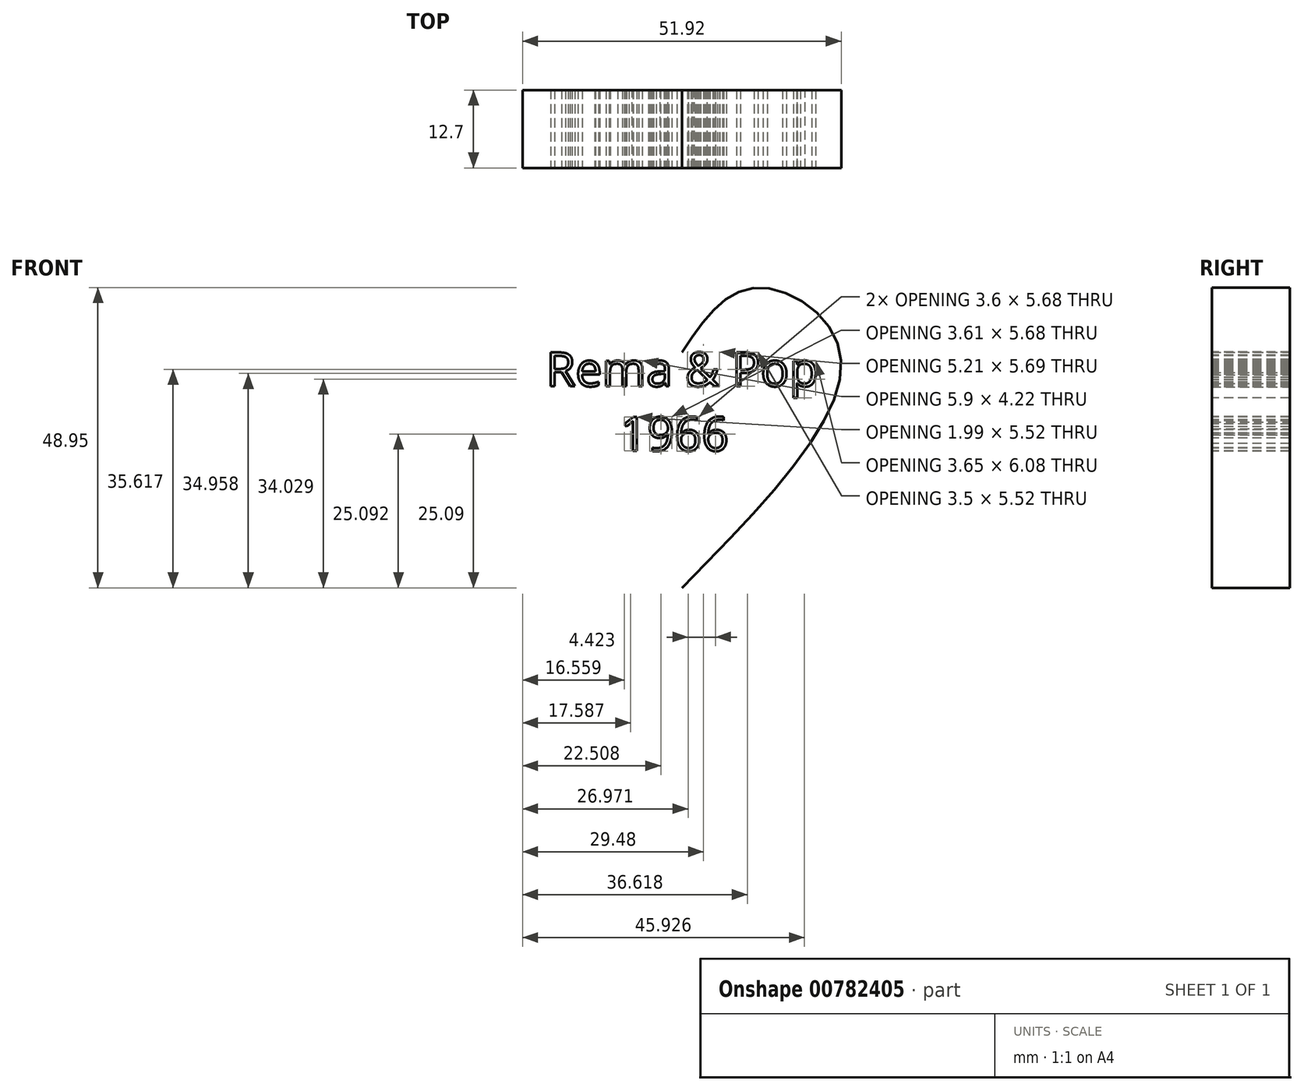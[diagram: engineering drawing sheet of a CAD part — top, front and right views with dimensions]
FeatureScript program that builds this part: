
annotation { "Feature Type Name" : "Feature", "Feature Type Description" : "" }
export const myFeature = defineFeature(function(context is Context, id is Id, definition is map)
    precondition{}
    {
        {
            var Q0;
            Q0=qCreatedBy(makeId("Front.planeOp"),FACE);
            var sketch = newSketch(context, id + "F0", { "sketchPlane" : qUnion([Q0])});
            skFitSpline(sketch, "E0", {"points": [v(0, 0) * mm, v(11.94, 10.5) * mm, v(25.76, 0) * mm, v(0, -38.42) * mm], "startDerivative": vector(38.37, 56.93) * mm, "endDerivative": vector(-91.66, -93.31) * mm});
            skFitSpline(sketch, "E1.MirrorCS", {"points": [v(0, 0) * mm, v(-11.94, 10.5) * mm, v(-25.76, 0) * mm, v(0, -38.42) * mm], "startDerivative": vector(-38.37, 56.93) * mm, "endDerivative": vector(91.66, -93.31) * mm});
            skSolve(sketch);
        }
        {
            var Q0;
            Q0=makeQuery(id+"F0.imprint","IMPRINT",FACE,{"disambiguationData":[TD([[makeQuery(id+"F0.imprint","IMPRINT",EDGE,{"derivedFrom":sQuery(id+"F0.wireOp",EDGE,"E0")}),-1.0]])]});
            extrude(context, id + "F1", {"entities" : qUnion([Q0]), "depth" : 12.7 * mm, "offsetDistance" : 25.4 * mm});
        }
        {
            var Q0;
            Q0=makeQuery(id+"F1.opExtrude","CAP_FACE",FACE,{"disambiguationData":[OSD([sQuery(id+"F0.wireOp",EDGE,"E0"),sQuery(id+"F0.wireOp",EDGE,"E1.MirrorCS")])],"isStart":false});
            var sketch = newSketch(context, id + "F2", { "sketchPlane" : qUnion([Q0])});
            skText(sketch, "E2", { "text": "Rema & Pop\n      1966", "fontName": "OpenSans-Regular.ttf"});
            const initialGuessF2  = {"E2": [-0.02214, -0.00557, 1, 0, 0.00557]};
            skSetInitialGuess(sketch, initialGuessF2);
            skSolve(sketch);
        }
        {
            var Q0;
            Q0 = qSketchRegion(id + "F2", true);
            extrude(context, id + "F3", {"entities" : qUnion([Q0]), "operationType" : NewBodyOperationType.REMOVE, "oppositeDirection" : true, "depth" : 25.4 * mm, "offsetDistance" : 25.4 * mm});
        }
    });
